# Revit family: RN 57034 Optifitt-Press-Übergang
name_source: partatom
category: Rohrformteile
units: mm (PartAtom-declared; Revit-internal decimal feet)

## family parameters
Arbeitsebenenbasiert = Nein
Beim Laden mit Abzugskörper schneiden = Nein
Bemaßung runder Anschluss = Durchmesser verwenden
Gemeinsam genutzt = Nein
Immer vertikal = Ja
Teiletyp = Verbindung

## types (5) — shared parameters
1.010.00.2 Blattnummer der Richtlinie = 29
1.010.00.3 Ausgabedatum (Monat) der Richtlinie = 201308
1.010.00.4 Herstellername = R. Nussbaum AG
1.010.00.5 Revisionsdatum der Datei = 20190521
1.010.00.6 Webadresse des Herstellers = http://www.nussbaum.ch
1.100.00.4 Produktbezeichnung = Versorgung
1.110.00.2 Index = 2
1.110.00.4 Produktbezeichnung = Optifitt-Press
1.960/3L.00.8 Link (URL) = https://www.nussbaum.ch
29.700.00.4 Produktname = Optifitt-Press-Übergang, mit Einsteckende und Innengewinde
29.700.00.5 Produktkennung = 2
29.700.00.6 Querschnittsform = 1
29.700.00.7 Nennweitensystem = DN
29.700.00.8 Nenndrucksystem = PN
29.710.02.4 Nenndruck = 16
29.710.02.5 max. zul. Überdruck [hPa] = 1600
29.710.02.7 max. zul. Dauer-Betriebsdruck [hPa] = 1600
29.710.02.9 max. zul. Dauer-Betriebstemperatur [°C] = 95
Beschreibung = Optifitt-Press-Übergang
Connector Visibility = Nein
EnclosingSpace Visibility = Nein
Hersteller = R. Nussbaum AG
URL = https://www.nussbaum.ch

## per-type parameters (varying)
| type | 1.800.00.3 TGA-Nummer | 1.800.00.4 Kommentarfeld | 1.810.00.3 Hersteller-Bestellnummer | 1.810.00.4 DATANORM-Nummer | 1.810.00.6 GTIN-Nummer | 29.710.02.10 Formstück-Gewicht [kg] | 29.710.02.3 Benennung | CONNECTOR0_DIAMETER_dX_0r | CONNECTOR0_dX_01 | CONNECTOR0_ref_dX | CONNECTOR1_DIAMETER_dX_0r | CONNECTOR1_dX_00 | CONNECTOR1_dX_01 | CONNECTOR1_ref_dX | Modell | R. Nussbaum AG 57034.25 de Visibility | R. Nussbaum AG 57034.26 de Visibility | R. Nussbaum AG 57034.27 de Visibility | R. Nussbaum AG 57034.28 de Visibility | R. Nussbaum AG 57034.29 de Visibility | Typenkommentare |
| DN=1 | 01900200000000000000000000000000000000000000000026000000000000000005 | 57034.29, Optifitt-Press-Übergang, mit Einsteckende und Innengewinde, DN=32, L=64, Rp=1 | 57034.29 | 57034.29 | 7612945816658 | 0.269 | Optifitt-Press-Übergang, mit Einsteckende und Innengewinde, DN=32, L=64, Rp=1 | 32 mm | 45 mm | 45 mm | 25 mm  [stored 0.082021 ft] | 47 mm | 64 mm | 47 mm | 57034.29 | Nein | Nein | Nein | Nein | Ja | Optifitt-Press-Übergang  DN=32 |
| DN=2 | 01900200000000000000000000000000000000000000000026000000000000000004 | 57034.28, Optifitt-Press-Übergang, mit Einsteckende und Innengewinde, DN=32, L=64, Rp=¾ | 57034.28 | 57034.28 | 7612945816641 | 0.296 | Optifitt-Press-Übergang, mit Einsteckende und Innengewinde, DN=32, L=64, Rp=¾ | 32 mm | 48 mm | 48 mm | 20 mm | 49 mm | 64 mm | 49 mm | 57034.28 | Nein | Nein | Nein | Ja | Nein | Optifitt-Press-Übergang  DN=32 |
| DN=32 | 01900200000000000000000000000000000000000000000026000000000000000003 | 57034.27, Optifitt-Press-Übergang, mit Einsteckende und Innengewinde, DN=32, L=64, Rp=½ | 57034.27 | 57034.27 | 7612945816634 | 0.311 | Optifitt-Press-Übergang, mit Einsteckende und Innengewinde, DN=32, L=64, Rp=½ | 32 mm | 49 mm | 49 mm | 15 mm | 51 mm | 64 mm | 51 mm | 57034.27 | Nein | Nein | Ja | Nein | Nein | Optifitt-Press-Übergang  DN=32 |
| DN=3 | 01900200000000000000000000000000000000000000000026000000000000000002 | 57034.26, Optifitt-Press-Übergang, mit Einsteckende und Innengewinde, DN=25, L=52, Rp=¾ | 57034.26 | 57034.26 | 7612945816627 | 0.147 | Optifitt-Press-Übergang, mit Einsteckende und Innengewinde, DN=25, L=52, Rp=¾ | 25 mm  [stored 0.082021 ft] | 35 mm | 35 mm | 20 mm | 37 mm | 52 mm | 37 mm | 57034.26 | Nein | Ja | Nein | Nein | Nein | Optifitt-Press-Übergang  DN=25 |
| DN=25 | 01900200000000000000000000000000000000000000000026000000000000000001 | 57034.25, Optifitt-Press-Übergang, mit Einsteckende und Innengewinde, DN=25, L=52, Rp=½ | 57034.25 | 57034.25 | 7612945816610 | 0.166 | Optifitt-Press-Übergang, mit Einsteckende und Innengewinde, DN=25, L=52, Rp=½ | 25 mm  [stored 0.082021 ft] | 37 mm | 37 mm | 15 mm | 39 mm  [stored 0.127953 ft] | 52 mm | 39 mm  [stored 0.127953 ft] | 57034.25 | Ja | Nein | Nein | Nein | Nein | Optifitt-Press-Übergang  DN=25 |

note: [stored X ft] marks values corroborated as IEEE doubles in the binary element streams (Revit-internal decimal feet)

## geometry (parser evidence)
native form markers: Sweep x2
no freeform markers — native parametric forms only
